# Revit family: Grohe_PlumbingFixtures_GrohthermSmartControl_TwoValveThermostat_29119DL0xxx
name_source: partatom
category: Plumbing Fixtures
units: mm (PartAtom-declared; Revit-internal decimal feet)

## family parameters
Cut with Voids When Loaded = No
Host = Face
OmniClass Number = 23.65.05.11.11
OmniClass Title = Water Supply Systems
Part Type = Normal
Room Calculation Point = No
Round Connector Dimension = Use Diameter
Shared = No

## types (1)
- 29119DL0
    Assembly Code = D2010
    AssetType = Fixed
    BIMObjectName = Grohe_PlumbingFixtures_GrohthermSmartControl_TwoValveThermostat_29119DL0
    CO2NeutralProduction = GROHE is one of the first leading manufacturer within the sanitary industry having a CO2-neutral production.
    CW Connection = No
    ClassificationName = Uniclass2015
    ClassificationValue = Pr_65_54_95_88
    Color = Other
    Cost = 0 $
    Default Elevation = 800 mm
    Description = set for final installation for GROHE Rapido SmartBox (35 600/35 604)
metal wall escutcheon with GROHE FastFixation 
(covered escutcheon and shaft sealing, covered 
fixing), retroactively 6° adjustable
GROHE StarLight finish
GROHE SmartControl push for ON-OFF, turn for volume adjustment from EcoJoy to Full Flow, exchangeable symbols
GROHE TurboStat compact cartridge with wax thermoelement
GROHE SafeStop safety button at 38°C
GROHE SafeStop Plus optional temperature limiter at 43°C or 46°C included
built-in non return valves and dirt strainers
multiple outlets can be run simultaneously
without roughing-in set
flow performance: 
outlet B = 24 l/min 
outlet C = 26 l/min
outlet B+C = 29 l/min
    DimensionsDocumentLink = https://cdn.cloud.grohe.com
    DocumentationCertificates = https://www.bimstore.co
    DocumentationInstallationGuide = https://www.bimstore.co
    DocumentationLiterature = https://www.bimstore.co
    DocumentationMaintenance = https://www.bimstore.co
    DocumentationTechnical = https://www.bimstore.co
    DurationUnit = Year
    EF000010 = EV022195
    EF002149 = Yes
    EF002286 = Insert (push coupling)
    EF002671 = Other
    EF005464 = 0
    EF011775 = EB
    EF011779 = Yes
    EF012753 = 29.0
    EF020105 = Yes
    EF020780 = Single-grip
    EF020781 = Other
    EF020782 = Brass
    EF020783 = Other
    EF020784 = Other
    EF020785 = M26 x 1.5
    EF020786 = 2
    EF020787 = Group I,<= 20 dB(A)
    EF020789 = 0 mm  [stored 0 ft]
    EF021827 = 29.0
    EF022042 = C
    EF023686 = Aluminium
    EF023687 = No
    EF023957 = Yes
    EFDE0022 = Group I, <=20 dB(A)
    Ecojoy = No
    ExpectedLife = 0
    FullRecyclabilityOfPlastic = All plastic components are fully recycable
    GROHESocialCommittment = green.grohe.com/social_engagement
    GROHESustainability = green.grohe.com
    HW Connection = No
    IfcExportAs = IfcPipeFitting
    IfcExportType = IfcPipeFittingType
    Keynote = N13
    Manufacturer = Grohe
    ManufacturerName = Grohe
    Material = Brass
    Model = 29119DL0
    ModelNumber = 29119DL0
    ModelReference = Thermostat for concealed installation with 2 valves
    NBSDescription = Thermostatic mixing valves
    NBSObjectName = Grohe - Thermostatic mixing valves
    NBSReference = 90-10-90/370
    NominalDepth = 0 mm  [stored 0 ft]
    NominalHeight = 0 mm  [stored 0 ft]
    NominalLength = 0 mm  [stored 0 ft]
    PQDiagramLink = https://cdn.cloud.grohe.com
    PrimaryMaterial = Grohe - Metal - Brushed Warm Sunset
    ProductDescription = set for final installation for GROHE Rapido SmartBox (35 600/35 604)
metal wall escutcheon with GROHE FastFixation 
(covered escutcheon and shaft sealing, covered 
fixing), retroactively 6° adjustable
GROHE StarLight finish
GROHE SmartControl push for ON-OFF, turn for volume adjustment from EcoJoy to Full Flow, exchangeable symbols
GROHE TurboStat compact cartridge with wax thermoelement
GROHE SafeStop safety button at 38°C
GROHE SafeStop Plus optional temperature limiter at 43°C or 46°C included
built-in non return valves and dirt strainers
multiple outlets can be run simultaneously
without roughing-in set
flow performance: 
outlet B = 24 l/min 
outlet C = 26 l/min
outlet B+C = 29 l/min
    ProductNumber = 29119DL0
    ProductShortText = Thermostat for concealed installation with 2 valves
Thermostat
    ProductType = Thermostat
    ProductionYear = 2021
    SustainabilityAward = green.grohe.com/awards
    SustainabilityReport = green.grohe.com/reporting
    TPIDocumentLink = https://cdn.cloud.grohe.com
    Type Comments = Thermostat for concealed installation with 2 valves
    TypeName = Thermostat for concealed installation with 2 valves
    URL = https://www.grohe.co.uk
    Vent Connection = No
    WarrantyDurationLabor = 0
    WarrantyDurationParts = 0
    WarrantyDurationUnit = Year
    Waste Connection = No
    _BSBibleVersion = 16
    _BimSpecGuid = 0
    _CurrentRevision = 1
    _DistributedBy = https://www.bimstore.co
    _ObjectUserGuide = https://www.bimstore.co

note: [stored X ft] marks values corroborated as IEEE doubles in the binary element streams (Revit-internal decimal feet)

## geometry (parser evidence)
native form markers: Sweep x3
no freeform markers — native parametric forms only
